# Revit family: FSL
name_source: partatom
category: Lighting Fixtures
revit_build: Autodesk Revit MEP 2012 (Build: 20110309_2315(x64)
units: mm (PartAtom-declared; Revit-internal decimal feet)

## types (1)
- FSL
    Apparent Load = 0 VA
    Default Elevation = 48.000"
    Description = Office buildings, monuments, facades, columns, flag poles, bridges, commercial, mixed retail, apartments, schools and campuses
    Finish = Bronze
    Lens = White Glass
    Manufacturer = Hubbell Lighting
    Manufacturer Fax = (866)-898-1065
    Model = FSL 10 LED Floodlight
    Photometric Web = Web ARF1 : ARF1-K-10L5K-070-W-U-DB
    Pivot Angle = 0.00°
    Pivot calc. = 90.00°
    Product Documentation Link = http://www.hubbelloutdoor.com
    Product Page URL = http://www.hubbelloutdoor.com
    Stand = Bronze
    Tilt Angle = 0.00°
    Total Input Wattage = 25 W
    URL = http://www.hubbelloutdoor.com
    Voltage = 120 V

## geometry (parser evidence)
native form markers: Blend x8, Sweep x9
no freeform markers — native parametric forms only
